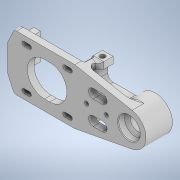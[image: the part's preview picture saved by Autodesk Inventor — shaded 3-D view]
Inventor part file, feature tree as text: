
AUTODESK INVENTOR PART (.ipt)
format: ipt  version: 2020 (Build 240168000, 168)  size: 713,216 bytes
history: native  units: in
note: dims shown in document units (in); Inventor stores cm internally (conversion verified against a paired STEP export)
features: extrude x21, sketch x21, projected_geometry x21, fillet x12, chamfer x5, reference x3, other x3, thicken_offset x2
ambient origin geometry x8: Origin, YZ Plane, XZ Plane, XY Plane, X Axis, Y Axis, Z Axis, Center Point
bodies: Solid1 (feature_tree)
feature tree (88):
  extrude  "Extrusion1"  Depth=1.6535in
  extrude  "Extrusion2"  Depth=1.6535in
  extrude  "Extrusion3"  Depth=0.1969in
  extrude  "Extrusion4"  Depth=0.1969in
  extrude  "Extrusion5"  Depth=0.5906in TaperAngle=0.0deg
  extrude  "Extrusion6"  Depth=0.315in
  extrude  "Extrusion7"  Depth=0.5906in TaperAngle=0.0deg
  chamfer  "Chamfer1"  Distance=0.1969in
  extrude  "Extrusion8"  Depth=0.1969in
  extrude  "Extrusion9"  Depth=0.7874in TaperAngle=45.0deg
  extrude  "Extrusion10"  Depth=0.126in
  chamfer  "Chamfer2"  Distance=0.7874in
  fillet  "Fillet1"  Radius=1.0236in
  fillet  "Fillet2"  Radius=0.7874in
  fillet  "Fillet3"  Radius=0.0787in
  fillet  "Fillet4"  Radius=1.0236in
  extrude  "Extrusion11"  Depth=0.7874in TaperAngle=45.0deg
  extrude  "Extrusion12"  Depth=0.0591in
  extrude  "Extrusion13"  Depth=0.1575in
  chamfer  "Chamfer3"  Distance=0.1378in
  extrude  "Extrusion14"  Depth=0.1181in
  fillet  "Fillet5"  Radius=0.0394in
  fillet  "Fillet6"  Radius=0.1378in
  chamfer  "Chamfer4"  Distance=0.2756in
  fillet  "Fillet7"  Radius=0.7874in
  fillet  "Fillet8"  Radius=0.1969in
  extrude  "Extrusion15"  Depth=0.1181in
  fillet  "Fillet9"  Radius=0.7874in
  extrude  "Extrusion16"  Depth=0.1181in
  extrude  "Extrusion17"  Depth=0.1181in
  extrude  "Extrusion18"  Depth=0.1969in
  extrude  "Extrusion19"  Depth=0.1181in TaperAngle=0.0deg
  fillet  "Fillet10"  Radius=0.1575in
  extrude  "Extrusion20"  Depth=0.1181in
  extrude  "Extrusion21"  Depth=0.1181in
  fillet  "Fillet11"  Radius=0.2756in
  fillet  "Fillet12"  Radius=0.1575in
  thicken_offset  "Thicken1"
  thicken_offset  "Thicken2"
  chamfer  "Chamfer5"  Distance=0.0394in
  sketch  "Sketch1"  dims[d0=2.4409in d1=1.6535in]
  reference  "Reference1"
  sketch  "Sketch2"  dims[d2=1.6535in d3=1.0236in]
  projected_geometry  "Projected Loop1"
  sketch  "Sketch3"  dims[d4=0.1969in d5=0.0in d6=1.0236in]
  projected_geometry  "Projected Loop2"
  reference  "Reference2"
  sketch  "Sketch4"  dims[d7=0.5906in d8=0.0in d9=0.1969in]
  projected_geometry  "Projected Loop3"
  projected_geometry  "Projected Loop4"
  projected_geometry  "Projected Loop5"
  sketch  "Sketch5"  dims[d10=1.6535in d11=0.5906in d12=0.0in]
  projected_geometry  "Projected Loop6"
  sketch  "Sketch6"  dims[d13=0.8661in d14=0.315in]
  sketch  "Sketch7"  dims[d15=1.1811in d16=0.5906in d17=0.0in]
  projected_geometry  "Projected Loop7"
  sketch  "Sketch8"  dims[d18=0.6299in d19=0.1969in d20=0.0in]
  projected_geometry  "Projected Loop8"
  sketch  "Sketch9"  dims[d21=0.1969in d22=0.0in d23=0.4724in]
  projected_geometry  "Projected Loop9"
  sketch  "Sketch10"  dims[d24=0.7874in d25=0.0in d26=0.0787in d27=0.0787in d28=45.0deg]
  projected_geometry  "Projected Loop10"
  sketch  "Sketch11"  dims[d29=0.0787in d30=0.126in]
  projected_geometry  "Projected Loop11"
  projected_geometry  "Projected Loop12"
  sketch  "Sketch12"  dims[d31=0.0787in]
  projected_geometry  "Projected Loop13"
  sketch  "Sketch13"  dims[d32=0.126in]
  projected_geometry  "Projected Loop14"
  sketch  "Sketch14"  dims[d33=0.0787in]
  projected_geometry  "Projected Loop15"
  sketch  "Sketch15"  dims[d34=0.126in]
  projected_geometry  "Projected Loop16"
  sketch  "Sketch16"  dims[d35=0.0787in]
  projected_geometry  "Projected Loop17"
  sketch  "Sketch17"  dims[d36=0.126in d37=0.7874in d38=0.0in d39=1.0236in d40=0.7874in d41=0.0in d42=0.0787in d43=1.0236in]
  projected_geometry  "Projected Loop18"
  sketch  "Sketch18"  dims[d44=0.7874in d45=0.0in d46=0.0787in d47=0.0787in d48=45.0deg]
  reference  "Reference3"
  projected_geometry  "Projected Loop19"
  sketch  "Sketch19"  dims[d49=0.0591in d50=0.1575in]
  projected_geometry  "Projected Loop20"
  sketch  "Sketch20"  dims[d51=0.1575in d52=0.1575in]
  projected_geometry  "Projected Loop21"
  sketch  "Sketch21"  dims[d53=0.0394in d54=0.1378in d55=0.2756in d56=0.0394in d57=0.1378in d58=0.2756in d59=0.7874in d60=0.0in d61=0.1969in d62=0.1575in d63=0.7874in d64=0.0in d65=0.0787in d66=0.4724in d67=0.1969in d68=0.2756in d69=0.0in d70=0.1575in d71=0.0787in d72=45.0deg d73=0.1181in d74=0.2756in d75=0.2756in d76=0.0in d77=0.1575in d78=0.0394in d79=0.0394in d80=0.0787in d81=45.0deg d82=0.0394in d83=0.0787in d84=0.1575in d85=0.1575in d86=0.1969in d87=0.0in d88=0.0394in d89=0.6693in d90=0.5906in d91=0.1181in d92=0.1181in d93=1.1811in d94=0.0in d95=0.1575in d96=1.6535in d97=0.1969in d98=0.0in d99=0.3937in d100=0.1969in d101=0.7874in d102=0.7874in d103=0.0in d104=0.1969in d105=0.0in d106=0.315in d107=0.2362in d108=0.2362in d109=0.1575in d110=0.1575in d111=0.1969in d112=0.0in d113=0.1575in d114=0.1969in d115=0.0in d116=0.0394in d117=0.1181in d118=0.0059in d119=0.0059in d120=0.0059in d121=0.0059in d122=0.0197in d123=0.0787in d124=45.0deg]
  parser-record x1  (decoder bookkeeping rows leaked as tree rows — omitted from the tree; the rows remain in map.json)
  other  "arm_shift_1.iam"
  other  "Nema17 Stepper Motor:1"
note: 1 file-system path scrubbed to <path> (originals preserved in map.json)
